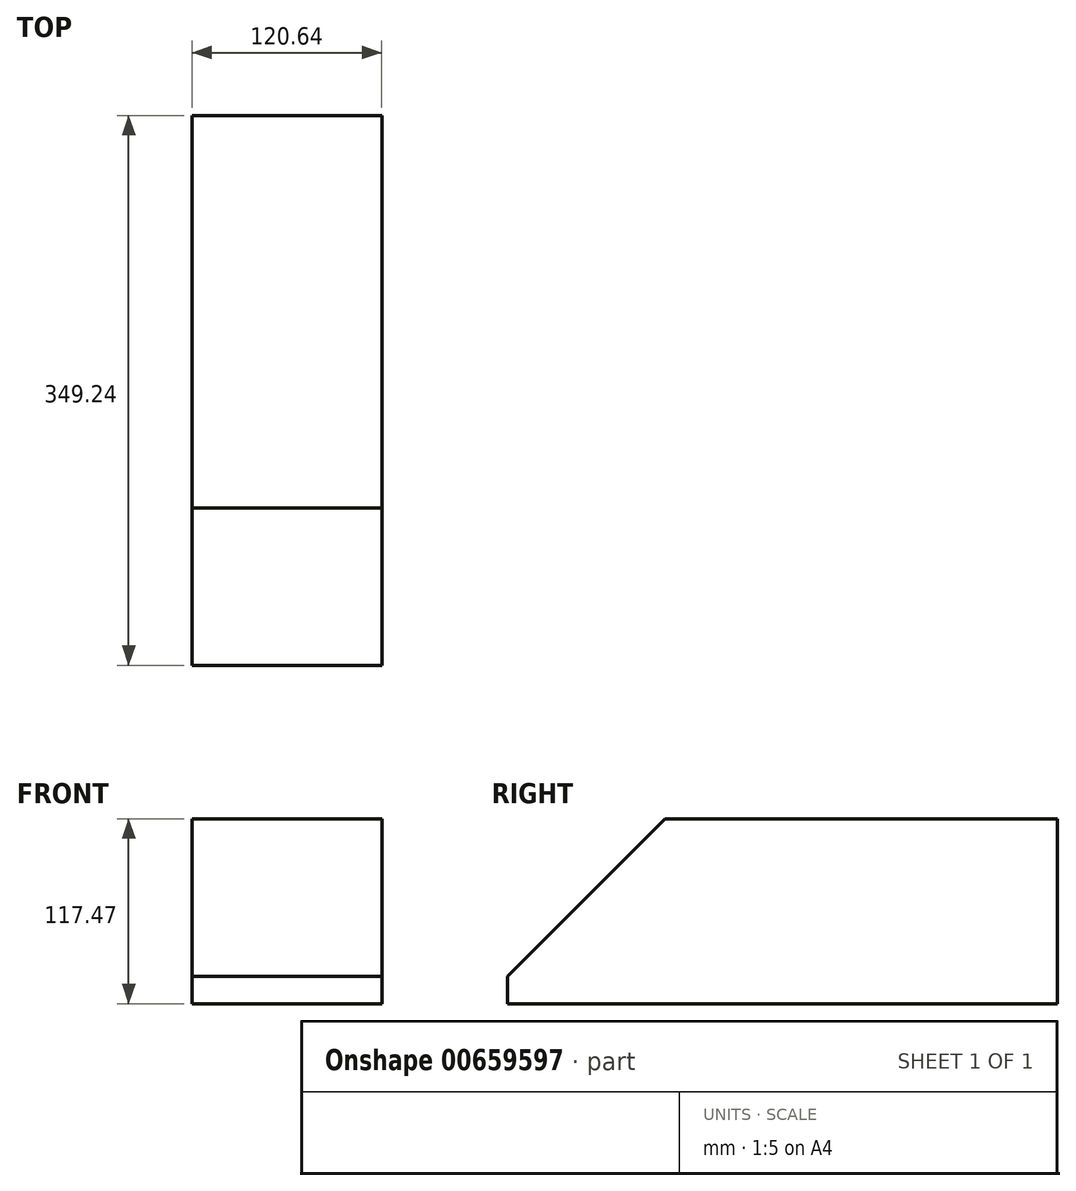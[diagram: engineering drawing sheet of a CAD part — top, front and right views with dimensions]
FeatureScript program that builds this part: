
annotation { "Feature Type Name" : "Feature", "Feature Type Description" : "" }
export const myFeature = defineFeature(function(context is Context, id is Id, definition is map)
    precondition{}
    {
        {
            var Q0;
            Q0=qCreatedBy(makeId("Top.planeOp"),FACE);
            var sketch = newSketch(context, id + "F0", { "sketchPlane" : qUnion([Q0])});
            skLineSegment(sketch, "E0.bottom", {"start": v(60.32, -174.63) * mm, "end": v(-60.33, -174.63) * mm});
            skLineSegment(sketch, "E0.top", {"start": v(60.33, 174.63) * mm, "end": v(-60.33, 174.63) * mm});
            skLineSegment(sketch, "E0.left", {"start": v(60.32, -174.63) * mm, "end": v(60.32, 174.63) * mm});
            skLineSegment(sketch, "E0.right", {"start": v(-60.33, -174.63) * mm, "end": v(-60.33, 174.63) * mm});
            skPoint(sketch, "E0.middle", {"position": v(0, 0) * mm});
            skSolve(sketch);
        }
        {
            var Q0;
            Q0=makeQuery(id+"F0.imprint","IMPRINT",FACE,{"disambiguationData":[TD([[makeQuery(id+"F0.imprint","IMPRINT",EDGE,{"derivedFrom":sQuery(id+"F0.wireOp",EDGE,"E0.bottom")}),-1.0]])]});
            extrude(context, id + "F1", {"entities" : qUnion([Q0]), "depth" : 117.47 * mm, "offsetDistance" : 25 * mm});
        }
        {
            var Q0;
            Q0=makeQuery(id+"F1.opExtrude","CAP_EDGE",EDGE,{"disambiguationData":[OSD([sQuery(id+"F0.wireOp",EDGE,"E0.bottom")])],"isStart":false});
            chamfer(context, id + "F2", {"entities" : qUnion([Q0]), "width" : 100 * mm, "tangentPropagation" : true});
        }
    });
